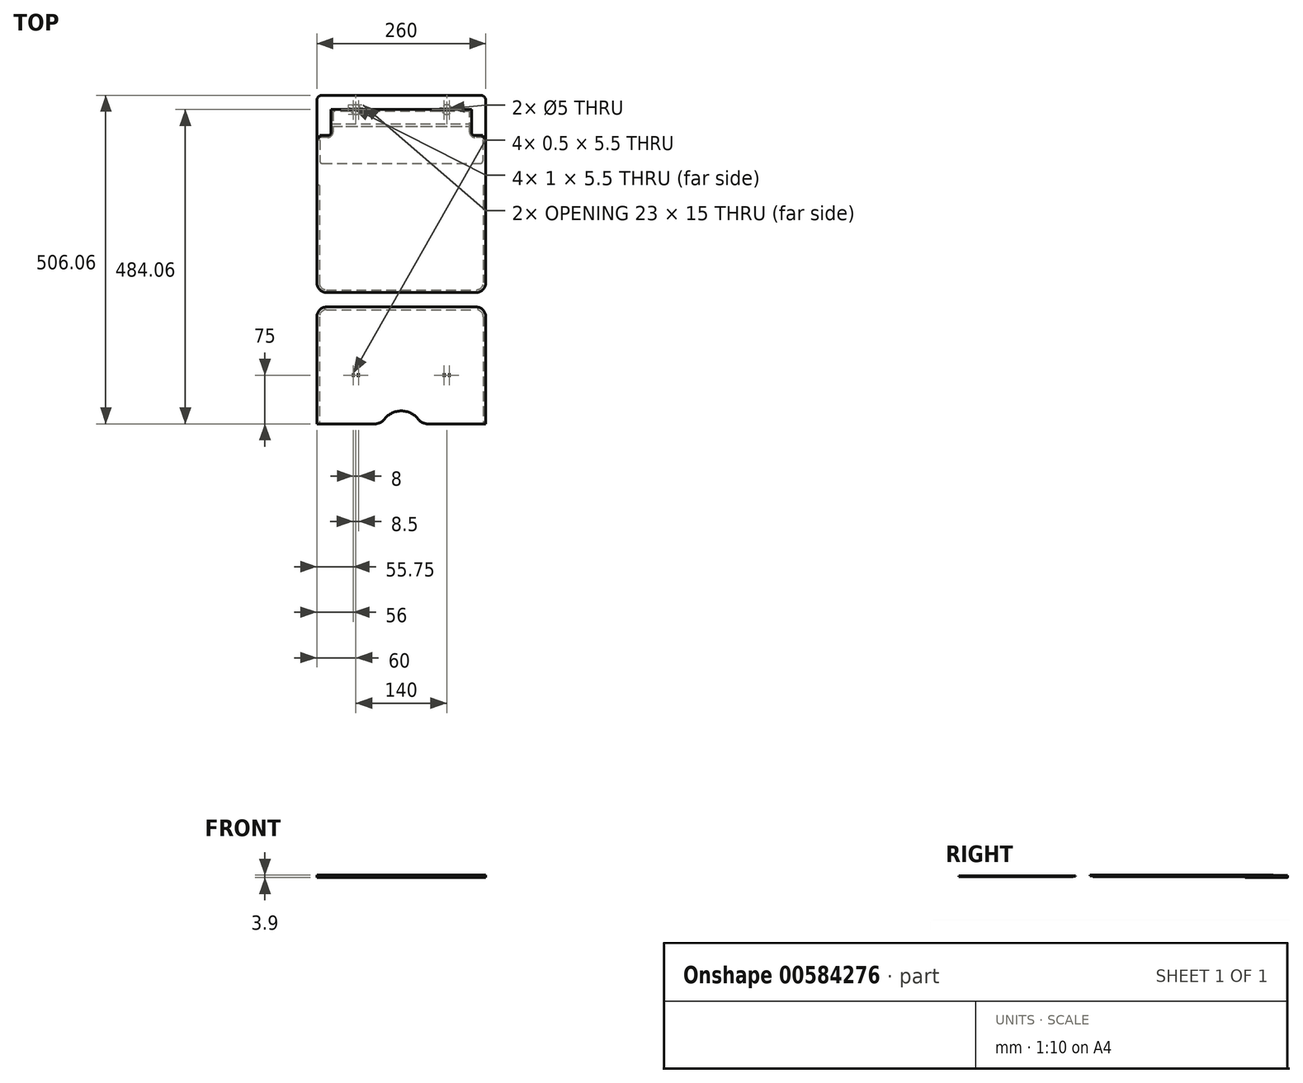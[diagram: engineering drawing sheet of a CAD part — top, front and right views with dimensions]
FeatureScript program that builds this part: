
annotation { "Feature Type Name" : "Feature", "Feature Type Description" : "" }
export const myFeature = defineFeature(function(context is Context, id is Id, definition is map)
    precondition{}
    {
        {
            var Q0;
            Q0=qCreatedBy(makeId("Top.planeOp"),FACE);
            var sketch = newSketch(context, id + "F0", { "sketchPlane" : qUnion([Q0])});
            skLineSegment(sketch, "E0.bottom", {"start": v(122, 253.03) * mm, "end": v(-122, 253.03) * mm});
            skLineSegment(sketch, "E0.top", {"start": v(-41.23, -253.03) * mm, "end": v(-130, -253.03) * mm});
            skLineSegment(sketch, "E0.left", {"start": v(130, 245.03) * mm, "end": v(130, 129.37) * mm});
            skLineSegment(sketch, "E0.right", {"start": v(-130, 245.03) * mm, "end": v(-130, 129.37) * mm});
            skPoint(sketch, "E0.middle", {"position": v(0, 0) * mm});
            skPoint(sketch, "E1", {"position": v(130, 147.97) * mm});
            skLineSegment(sketch, "E2", {"start": v(130, 188.1) * mm, "end": v(113.2, 188.1) * mm});
            skLineSegment(sketch, "E3", {"start": v(105.2, 196.1) * mm, "end": v(105.2, 228.22) * mm});
            skLineSegment(sketch, "E4", {"start": v(105.2, 228.22) * mm, "end": v(-105.2, 228.22) * mm});
            skLineSegment(sketch, "E5", {"start": v(-105.2, 228.22) * mm, "end": v(-105.2, 196.1) * mm});
            skLineSegment(sketch, "E6", {"start": v(-113.2, 188.1) * mm, "end": v(-130, 188.1) * mm});
            skLineSegment(sketch, "E7", {"start": v(-60.78, 228.22) * mm, "end": v(-60.78, 253.03) * mm, "construction": true});
            skPoint(sketch, "E8.visualSharp", {"position": v(-130, 253.03) * mm});
            skArc(sketch, "E8.filletArc", {"start": v(-122, 253.03) * mm, "mid": v(-127.66, 250.69) * mm, "end": v(-130, 245.03) * mm});
            skPoint(sketch, "E9.visualSharp", {"position": v(130, 253.03) * mm});
            skArc(sketch, "E9.filletArc", {"start": v(130, 245.03) * mm, "mid": v(127.66, 250.69) * mm, "end": v(122, 253.03) * mm});
            skPoint(sketch, "E10.visualSharp", {"position": v(105.2, 188.1) * mm});
            skArc(sketch, "E10.filletArc", {"start": v(105.2, 196.1) * mm, "mid": v(107.54, 190.43) * mm, "end": v(113.2, 188.1) * mm});
            skPoint(sketch, "E11.visualSharp", {"position": v(-105.2, 188.1) * mm});
            skArc(sketch, "E11.filletArc", {"start": v(-113.2, 188.1) * mm, "mid": v(-107.54, 190.43) * mm, "end": v(-105.2, 196.1) * mm});
            skLineSegment(sketch, "E12", {"start": v(-130, 179) * mm, "end": v(-105.2, 179) * mm, "construction": true});
            skLineSegment(sketch, "E13", {"start": v(130, 147.97) * mm, "end": v(-130, 147.97) * mm, "construction": true});
            skArc(sketch, "E14", {"start": v(25.52, -245.41) * mm, "mid": v(0, -233.03) * mm, "end": v(-25.52, -245.41) * mm});
            skPoint(sketch, "E15.newPointA", {"position": v(-30, -253.03) * mm});
            skPoint(sketch, "E15.newPointB", {"position": v(130, -253.03) * mm});
            skArc(sketch, "E15.filletArc", {"start": v(-41.23, -253.03) * mm, "mid": v(-32.5, -251.02) * mm, "end": v(-25.52, -245.41) * mm});
            skLineSegment(sketch, "E16", {"start": v(41.23, -253.03) * mm, "end": v(132.5, -253.03) * mm});
            skPoint(sketch, "E17.visualSharp", {"position": v(30, -253.03) * mm});
            skArc(sketch, "E17.filletArc", {"start": v(25.52, -245.41) * mm, "mid": v(32.5, -251.02) * mm, "end": v(41.23, -253.03) * mm});
            skLineSegment(sketch, "E18.0", {"start": v(-113.2, 191.1) * mm, "end": v(-125.5, 191.1) * mm});
            skArc(sketch, "E18.1", {"start": v(-113.2, 191.1) * mm, "mid": v(-109.66, 192.55) * mm, "end": v(-108.2, 196.1) * mm});
            skLineSegment(sketch, "E18.2", {"start": v(-108.2, 231.22) * mm, "end": v(-108.2, 196.1) * mm});
            skLineSegment(sketch, "E18.3", {"start": v(125.5, 191.1) * mm, "end": v(113.2, 191.1) * mm});
            skArc(sketch, "E18.4", {"start": v(108.2, 196.1) * mm, "mid": v(109.66, 192.55) * mm, "end": v(113.2, 191.1) * mm});
            skLineSegment(sketch, "E18.5", {"start": v(108.2, 196.1) * mm, "end": v(108.2, 231.22) * mm});
            skLineSegment(sketch, "E18.6", {"start": v(108.2, 231.22) * mm, "end": v(-108.2, 231.22) * mm});
            skLineSegment(sketch, "E19", {"start": v(-125.5, 191.1) * mm, "end": v(-125.5, 188.1) * mm});
            skLineSegment(sketch, "E20.MirrorCS", {"start": v(125.5, 191.1) * mm, "end": v(125.5, 188.1) * mm});
            skLineSegment(sketch, "E21", {"start": v(-115, -73.03) * mm, "end": v(115, -73.03) * mm});
            skLineSegment(sketch, "E22", {"start": v(-115, -50.63) * mm, "end": v(115, -50.63) * mm});
            skArc(sketch, "E23.filletArc", {"start": v(-130, -35.63) * mm, "mid": v(-125.6, -46.24) * mm, "end": v(-115, -50.63) * mm});
            skArc(sketch, "E24.filletArc", {"start": v(115, -50.63) * mm, "mid": v(125.6, -46.24) * mm, "end": v(130, -35.63) * mm});
            skLineSegment(sketch, "E25", {"start": v(-130, -88.03) * mm, "end": v(-130, -253.03) * mm});
            skLineSegment(sketch, "E26", {"start": v(130, -88.03) * mm, "end": v(130, -253.03) * mm});
            skPoint(sketch, "E27.visualSharp", {"position": v(-130, -73.03) * mm});
            skArc(sketch, "E27.filletArc", {"start": v(-115, -73.03) * mm, "mid": v(-125.6, -77.42) * mm, "end": v(-130, -88.03) * mm});
            skPoint(sketch, "E28.visualSharp", {"position": v(130, -73.03) * mm});
            skArc(sketch, "E28.filletArc", {"start": v(130, -88.03) * mm, "mid": v(125.6, -77.42) * mm, "end": v(115, -73.03) * mm});
            skLineSegment(sketch, "E29.bottom", {"start": v(-74.25, -175.28) * mm, "end": v(-73.75, -175.28) * mm});
            skLineSegment(sketch, "E29.top", {"start": v(-74.25, -180.78) * mm, "end": v(-73.75, -180.78) * mm});
            skLineSegment(sketch, "E29.left", {"start": v(-74.25, -175.28) * mm, "end": v(-74.25, -180.78) * mm});
            skLineSegment(sketch, "E29.right", {"start": v(-73.75, -175.28) * mm, "end": v(-73.75, -180.78) * mm});
            skLineSegment(sketch, "E30", {"start": v(-70, -182.22) * mm, "end": v(-70, -190.86) * mm, "construction": true});
            skPoint(sketch, "E31.orphan", {"position": v(-90.2, -187.28) * mm});
            skLineSegment(sketch, "E32.MirrorCS", {"start": v(-65.75, -180.78) * mm, "end": v(-66.25, -180.78) * mm});
            skLineSegment(sketch, "E33.MirrorCS", {"start": v(-66.25, -175.28) * mm, "end": v(-66.25, -180.78) * mm});
            skLineSegment(sketch, "E34.MirrorCS", {"start": v(-65.75, -175.28) * mm, "end": v(-65.75, -180.78) * mm});
            skLineSegment(sketch, "E35.MirrorCS", {"start": v(-65.75, -175.28) * mm, "end": v(-66.25, -175.28) * mm});
            skPoint(sketch, "E36", {"position": v(-70, -178.03) * mm});
            skLineSegment(sketch, "E37.trimOffspring", {"start": v(-73.75, -178.03) * mm, "end": v(-66.25, -178.03) * mm, "construction": true});
            skPoint(sketch, "E38.trimOffspring.end.orphan", {"position": v(-65.68, -178.03) * mm});
            skPoint(sketch, "E39.start.orphan", {"position": v(-74.32, -178.03) * mm});
            skLineSegment(sketch, "E40.MirrorCS", {"start": v(74.25, -180.78) * mm, "end": v(73.75, -180.78) * mm});
            skLineSegment(sketch, "E41.MirrorCS", {"start": v(74.25, -175.28) * mm, "end": v(73.75, -175.28) * mm});
            skLineSegment(sketch, "E42.MirrorCS", {"start": v(65.75, -175.28) * mm, "end": v(66.25, -175.28) * mm});
            skLineSegment(sketch, "E43.MirrorCS", {"start": v(65.75, -180.78) * mm, "end": v(66.25, -180.78) * mm});
            skPoint(sketch, "E44.MirrorP", {"position": v(74.32, -178.03) * mm});
            skLineSegment(sketch, "E45.MirrorCS", {"start": v(65.75, -175.28) * mm, "end": v(65.75, -180.78) * mm});
            skLineSegment(sketch, "E46.MirrorCS", {"start": v(73.75, -178.03) * mm, "end": v(66.25, -178.03) * mm, "construction": true});
            skLineSegment(sketch, "E47.MirrorCS", {"start": v(73.75, -175.28) * mm, "end": v(73.75, -180.78) * mm});
            skPoint(sketch, "E48.MirrorP", {"position": v(70, -178.03) * mm});
            skLineSegment(sketch, "E49.MirrorCS", {"start": v(74.25, -175.28) * mm, "end": v(74.25, -180.78) * mm});
            skLineSegment(sketch, "E50.MirrorCS", {"start": v(66.25, -175.28) * mm, "end": v(66.25, -180.78) * mm});
            skPoint(sketch, "E51.MirrorP", {"position": v(65.68, -178.03) * mm});
            skLineSegment(sketch, "E52", {"start": v(-130, 129.37) * mm, "end": v(130, 129.37) * mm, "construction": true});
            skLineSegment(sketch, "E53", {"start": v(-130, 129.37) * mm, "end": v(-130, -35.63) * mm});
            skLineSegment(sketch, "E54", {"start": v(130, 129.37) * mm, "end": v(130, -35.63) * mm});
            skSolve(sketch);
        }
        {
            var Q0;
            {var subQ1=sQuery(id+"F0.wireOp",EDGE,"E0.top");Q0=makeQuery(id+"F0.imprint","IMPRINT",FACE,{"disambiguationData":[TD([[makeQuery(id+"F0.imprint","IMPRINT",EDGE,{"derivedFrom":subQ1}),-1.0]])]});}
            extrude(context, id + "F1", {"entities" : qUnion([Q0]), "oppositeDirection" : true, "depth" : 0.8 * mm, "offsetDistance" : 25 * mm});
        }
        {
            var Q0;
            Q0=makeQuery(id+"F0.imprint","IMPRINT",FACE,{"disambiguationData":[TD([[makeQuery(id+"F0.imprint","IMPRINT",EDGE,{"derivedFrom":sQuery(id+"F0.wireOp",EDGE,"E3")}),1.0]])]});
            var Q1;
            Q1=makeQuery(id+"F0.imprint","IMPRINT",FACE,{"disambiguationData":[TD([[makeQuery(id+"F0.imprint","IMPRINT",EDGE,{"derivedFrom":sQuery(id+"F0.wireOp",EDGE,"E3")}),-1.0]])]});
            extrude(context, id + "F2", {"entities" : qUnion([Q0, Q1]), "depth" : 0.9 * mm, "offsetDistance" : 25 * mm});
        }
        {
            var Q0;
            Q0=makeQuery(id+"F0.imprint","IMPRINT",FACE,{"disambiguationData":[TD([[makeQuery(id+"F0.imprint","IMPRINT",EDGE,{"derivedFrom":sQuery(id+"F0.wireOp",EDGE,"E0.bottom")}),1.0]])]});
            extrude(context, id + "F3", {"entities" : qUnion([Q0]), "oppositeDirection" : true, "depth" : 0.9 * mm, "offsetDistance" : 25 * mm});
        }
        {
            var Q0;
            Q0=makeQuery(id+"F0.imprint","IMPRINT",FACE,{"disambiguationData":[TD([[makeQuery(id+"F0.imprint","IMPRINT",EDGE,{"derivedFrom":sQuery(id+"F0.wireOp",EDGE,"E3")}),-1.0]])]});
            var Q1;
            Q1=makeQuery(id+"F0.imprint","IMPRINT",FACE,{"disambiguationData":[TD([[makeQuery(id+"F0.imprint","IMPRINT",EDGE,{"derivedFrom":sQuery(id+"F0.wireOp",EDGE,"E0.bottom")}),1.0]])]});
            extrude(context, id + "F4", {"entities" : qUnion([Q0, Q1]), "depth" : 0.6 * mm, "offsetDistance" : 25 * mm});
        }
        {
            var Q0;
            Q0=makeQuery(id+"F3.opExtrude","CAP_FACE",FACE,{"disambiguationData":[OSD([sQuery(id+"F0.wireOp",EDGE,"E0.bottom"),sQuery(id+"F0.wireOp",EDGE,"E0.left"),sQuery(id+"F0.wireOp",EDGE,"E0.right"),sQuery(id+"F0.wireOp",EDGE,"E2"),sQuery(id+"F0.wireOp",EDGE,"E6"),sQuery(id+"F0.wireOp",EDGE,"E8.filletArc"),sQuery(id+"F0.wireOp",EDGE,"E9.filletArc"),sQuery(id+"F0.wireOp",EDGE,"E18.0"),sQuery(id+"F0.wireOp",EDGE,"E18.2"),sQuery(id+"F0.wireOp",EDGE,"E18.3"),sQuery(id+"F0.wireOp",EDGE,"E18.5"),sQuery(id+"F0.wireOp",EDGE,"E18.6"),sQuery(id+"F0.wireOp",EDGE,"E19"),sQuery(id+"F0.wireOp",EDGE,"E20.MirrorCS")])],"isStart":false});
            var sketch = newSketch(context, id + "F5", { "sketchPlane" : qUnion([Q0])});
            skLineSegment(sketch, "E55.0", {"start": v(-130, -245.03) * mm, "end": v(-130, -188.1) * mm});
            skArc(sketch, "E56.0", {"start": v(-122, -253.03) * mm, "mid": v(-127.66, -250.69) * mm, "end": v(-130, -245.03) * mm});
            skLineSegment(sketch, "E57.0", {"start": v(122, -253.03) * mm, "end": v(-122, -253.03) * mm});
            skArc(sketch, "E58.0", {"start": v(130, -245.03) * mm, "mid": v(127.66, -250.69) * mm, "end": v(122, -253.03) * mm});
            skLineSegment(sketch, "E59.0", {"start": v(130, -245.03) * mm, "end": v(130, -188.1) * mm});
            skPoint(sketch, "E60.orphan", {"position": v(-130, -129.37) * mm});
            skPoint(sketch, "E61.orphan", {"position": v(130, -129.37) * mm});
            skLineSegment(sketch, "E62.0", {"start": v(-125.5, -191.1) * mm, "end": v(-125.5, -188.1) * mm});
            skLineSegment(sketch, "E63", {"start": v(-125.5, -183.96) * mm, "end": v(-125.5, -151.97) * mm});
            skArc(sketch, "E64", {"start": v(-125.86, -184.36) * mm, "mid": v(-128.28, -185.57) * mm, "end": v(-129.25, -188.1) * mm});
            skPoint(sketch, "E65.newPointB", {"position": v(-129.25, -188.1) * mm});
            skArc(sketch, "E66.filletArc", {"start": v(-125.86, -184.36) * mm, "mid": v(-125.6, -184.23) * mm, "end": v(-125.5, -183.96) * mm});
            skLineSegment(sketch, "E67.0", {"start": v(0, -147.97) * mm, "end": v(-121.5, -147.97) * mm});
            skPoint(sketch, "E68.newPointB", {"position": v(-130, -147.97) * mm});
            skArc(sketch, "E68.filletArc", {"start": v(-121.5, -147.97) * mm, "mid": v(-124.33, -149.14) * mm, "end": v(-125.5, -151.97) * mm});
            skPoint(sketch, "E69.orphan", {"position": v(130, -147.97) * mm});
            skLineSegment(sketch, "E70.MirrorCS", {"start": v(0, -147.97) * mm, "end": v(121.5, -147.97) * mm});
            skArc(sketch, "E71.MirrorCS", {"start": v(121.5, -147.97) * mm, "mid": v(124.33, -149.14) * mm, "end": v(125.5, -151.97) * mm});
            skLineSegment(sketch, "E72.MirrorCS", {"start": v(125.5, -183.96) * mm, "end": v(125.5, -151.97) * mm});
            skArc(sketch, "E73.MirrorCS", {"start": v(125.86, -184.36) * mm, "mid": v(125.6, -184.23) * mm, "end": v(125.5, -183.96) * mm});
            skArc(sketch, "E74.MirrorCS", {"start": v(125.86, -184.36) * mm, "mid": v(128.28, -185.57) * mm, "end": v(129.25, -188.1) * mm});
            skLineSegment(sketch, "E75", {"start": v(-130, -188.1) * mm, "end": v(-129.25, -188.1) * mm});
            skLineSegment(sketch, "E76", {"start": v(129.25, -188.1) * mm, "end": v(130, -188.1) * mm});
            skSolve(sketch);
        }
        {
            var Q0;
            Q0 = qSketchRegion(id + "F5", true);
            extrude(context, id + "F6", {"entities" : qUnion([Q0]), "depth" : 0.6 * mm, "offsetDistance" : 25 * mm});
        }
        {
            var Q0;
            Q0=makeQuery(id+"F6.opExtrude","CAP_FACE",FACE,{"disambiguationData":[OSD([sQuery(id+"F5.wireOp",EDGE,"E55.0"),sQuery(id+"F5.wireOp",EDGE,"E56.0"),sQuery(id+"F5.wireOp",EDGE,"E57.0"),sQuery(id+"F5.wireOp",EDGE,"E58.0"),sQuery(id+"F5.wireOp",EDGE,"E59.0"),sQuery(id+"F5.wireOp",EDGE,"mqd3fcgL-vkYM-jt8C-SEZb-QTAqxbzKtnkH"),sQuery(id+"F5.wireOp",EDGE,"E63"),sQuery(id+"F5.wireOp",EDGE,"E64"),sQuery(id+"F5.wireOp",EDGE,"E65.filletArc"),sQuery(id+"F5.wireOp",EDGE,"E66.filletArc"),sQuery(id+"F5.wireOp",EDGE,"E67.0"),sQuery(id+"F5.wireOp",EDGE,"E68.filletArc"),sQuery(id+"F5.wireOp",EDGE,"E70.MirrorCS"),sQuery(id+"F5.wireOp",EDGE,"E71.MirrorCS"),sQuery(id+"F5.wireOp",EDGE,"E72.MirrorCS"),sQuery(id+"F5.wireOp",EDGE,"E73.MirrorCS"),sQuery(id+"F5.wireOp",EDGE,"E74.MirrorCS"),sQuery(id+"F5.wireOp",EDGE,"eea31a7d-e614-436a-bde2-b2130c57034b0.MirrorCS"),sQuery(id+"F5.wireOp",EDGE,"bd1179cf-cb36-4206-b0af-3bf9bbb72a3d0.MirrorCS")])],"isStart":false});
            var sketch = newSketch(context, id + "F7", { "sketchPlane" : qUnion([Q0])});
            skLineSegment(sketch, "E77.0.0", {"start": v(-125.5, -188.1) * mm, "end": v(-125.5, -191.1) * mm});
            skLineSegment(sketch, "E77.0.1", {"start": v(-125.5, -191.1) * mm, "end": v(-113.2, -191.1) * mm});
            skArc(sketch, "E77.0.2", {"start": v(-113.2, -191.1) * mm, "mid": v(-109.66, -192.55) * mm, "end": v(-108.2, -196.1) * mm});
            skLineSegment(sketch, "E77.0.3", {"start": v(-108.2, -196.1) * mm, "end": v(-108.2, -209.03) * mm});
            skLineSegment(sketch, "E77.0.5", {"start": v(108.2, -209.03) * mm, "end": v(108.2, -196.1) * mm});
            skArc(sketch, "E77.0.6", {"start": v(108.2, -196.1) * mm, "mid": v(109.66, -192.55) * mm, "end": v(113.2, -191.1) * mm});
            skLineSegment(sketch, "E77.0.7", {"start": v(113.2, -191.1) * mm, "end": v(125.5, -191.1) * mm});
            skLineSegment(sketch, "E77.0.8", {"start": v(125.5, -191.1) * mm, "end": v(125.5, -188.1) * mm});
            skLineSegment(sketch, "E77.0.9", {"start": v(125.5, -188.1) * mm, "end": v(130, -188.1) * mm});
            skLineSegment(sketch, "E77.0.10", {"start": v(130, -188.1) * mm, "end": v(130, -245.03) * mm});
            skArc(sketch, "E77.0.11", {"start": v(130, -245.03) * mm, "mid": v(127.66, -250.69) * mm, "end": v(122, -253.03) * mm});
            skLineSegment(sketch, "E77.0.12", {"start": v(122, -253.03) * mm, "end": v(-122, -253.03) * mm});
            skArc(sketch, "E77.0.13", {"start": v(-122, -253.03) * mm, "mid": v(-127.66, -250.69) * mm, "end": v(-130, -245.03) * mm});
            skLineSegment(sketch, "E77.0.14", {"start": v(-130, -245.03) * mm, "end": v(-130, -188.1) * mm});
            skLineSegment(sketch, "E77.0.15", {"start": v(-130, -188.1) * mm, "end": v(-125.5, -188.1) * mm});
            skLineSegment(sketch, "E78", {"start": v(-108.2, -209.03) * mm, "end": v(108.2, -209.03) * mm});
            skPoint(sketch, "E77.0.4.end.orphan", {"position": v(108.2, -231.22) * mm});
            skPoint(sketch, "E77.0.4.start.orphan", {"position": v(-108.2, -231.22) * mm});
            skArc(sketch, "E79", {"start": v(-77.07, -233.53) * mm, "mid": v(-70, -238.53) * mm, "end": v(-62.93, -233.53) * mm});
            skLineSegment(sketch, "E80", {"start": v(-79, -231.03) * mm, "end": v(-61, -231.03) * mm, "construction": true});
            skLineSegment(sketch, "E81", {"start": v(-70, -233.39) * mm, "end": v(-70, -223.53) * mm, "construction": true});
            skArc(sketch, "E82.0.startCap", {"start": v(-79, -233.53) * mm, "mid": v(-81.5, -231.03) * mm, "end": v(-79, -228.53) * mm});
            skArc(sketch, "E82.0.endCap", {"start": v(-61, -228.53) * mm, "mid": v(-58.5, -231.03) * mm, "end": v(-61, -233.53) * mm});
            skLineSegment(sketch, "E82.0.left", {"start": v(-79, -228.53) * mm, "end": v(-77.07, -228.53) * mm});
            skLineSegment(sketch, "E82.0.right", {"start": v(-79, -233.53) * mm, "end": v(-77.07, -233.53) * mm});
            skLineSegment(sketch, "E83.trimOffspring", {"start": v(-62.93, -228.53) * mm, "end": v(-61, -228.53) * mm});
            skLineSegment(sketch, "E84.trimOffspring", {"start": v(-62.93, -233.53) * mm, "end": v(-61, -233.53) * mm});
            skArc(sketch, "E85.trimOffspring", {"start": v(-62.93, -228.53) * mm, "mid": v(-70, -223.53) * mm, "end": v(-77.07, -228.53) * mm});
            skArc(sketch, "E86.MirrorCS", {"start": v(77.07, -233.53) * mm, "mid": v(70, -238.53) * mm, "end": v(62.93, -233.53) * mm});
            skLineSegment(sketch, "E87.MirrorCS", {"start": v(79, -233.53) * mm, "end": v(77.07, -233.53) * mm});
            skArc(sketch, "E88.MirrorCS", {"start": v(79, -233.53) * mm, "mid": v(81.5, -231.03) * mm, "end": v(79, -228.53) * mm});
            skLineSegment(sketch, "E89.MirrorCS", {"start": v(79, -228.53) * mm, "end": v(77.07, -228.53) * mm});
            skArc(sketch, "E90.MirrorCS", {"start": v(62.93, -228.53) * mm, "mid": v(70, -223.53) * mm, "end": v(77.07, -228.53) * mm});
            skLineSegment(sketch, "E91.MirrorCS", {"start": v(62.93, -228.53) * mm, "end": v(61, -228.53) * mm});
            skArc(sketch, "E92.MirrorCS", {"start": v(61, -228.53) * mm, "mid": v(58.5, -231.03) * mm, "end": v(61, -233.53) * mm});
            skLineSegment(sketch, "E93.MirrorCS", {"start": v(62.93, -233.53) * mm, "end": v(61, -233.53) * mm});
            skSolve(sketch);
        }
        {
            var Q0;
            {var subQ1=sQuery(id+"F7.wireOp",EDGE,"E77.0.0");Q0=makeQuery(id+"F7.imprint","IMPRINT",FACE,{"disambiguationData":[TD([[makeQuery(id+"F7.imprint","IMPRINT",EDGE,{"derivedFrom":subQ1}),-1.0]])]});}
            extrude(context, id + "F8", {"entities" : qUnion([Q0]), "depth" : 0.9 * mm, "offsetDistance" : 25 * mm});
        }
        {
            var Q0;
            Q0=makeQuery(id+"F8.opExtrude","CAP_FACE",FACE,{"disambiguationData":[OSD([sQuery(id+"F5.wireOp",EDGE,"mqd3fcgL-vkYM-jt8C-SEZb-QTAqxbzKtnkH"),sQuery(id+"F5.wireOp",EDGE,"E65.filletArc"),sQuery(id+"F5.wireOp",EDGE,"eea31a7d-e614-436a-bde2-b2130c57034b0.MirrorCS"),sQuery(id+"F5.wireOp",EDGE,"bd1179cf-cb36-4206-b0af-3bf9bbb72a3d0.MirrorCS"),sQuery(id+"F7.wireOp",EDGE,"E77.0.0"),sQuery(id+"F7.wireOp",EDGE,"E77.0.1"),sQuery(id+"F7.wireOp",EDGE,"E77.0.2"),sQuery(id+"F7.wireOp",EDGE,"E77.0.3"),sQuery(id+"F7.wireOp",EDGE,"E77.0.5"),sQuery(id+"F7.wireOp",EDGE,"E77.0.6"),sQuery(id+"F7.wireOp",EDGE,"E77.0.7"),sQuery(id+"F7.wireOp",EDGE,"E77.0.8"),sQuery(id+"F7.wireOp",EDGE,"E77.0.9"),sQuery(id+"F7.wireOp",EDGE,"E77.0.10"),sQuery(id+"F7.wireOp",EDGE,"E77.0.11"),sQuery(id+"F7.wireOp",EDGE,"E77.0.12"),sQuery(id+"F7.wireOp",EDGE,"E77.0.13"),sQuery(id+"F7.wireOp",EDGE,"E77.0.14"),sQuery(id+"F7.wireOp",EDGE,"E77.0.15"),sQuery(id+"F7.wireOp",EDGE,"E78"),sQuery(id+"F7.wireOp",EDGE,"E79"),sQuery(id+"F7.wireOp",EDGE,"E82.0.startCap"),sQuery(id+"F7.wireOp",EDGE,"E82.0.endCap"),sQuery(id+"F7.wireOp",EDGE,"E82.0.left"),sQuery(id+"F7.wireOp",EDGE,"E82.0.right"),sQuery(id+"F7.wireOp",EDGE,"E83.trimOffspring"),sQuery(id+"F7.wireOp",EDGE,"E84.trimOffspring"),sQuery(id+"F7.wireOp",EDGE,"E85.trimOffspring"),sQuery(id+"F7.wireOp",EDGE,"E86.MirrorCS"),sQuery(id+"F7.wireOp",EDGE,"E87.MirrorCS"),sQuery(id+"F7.wireOp",EDGE,"E88.MirrorCS"),sQuery(id+"F7.wireOp",EDGE,"E89.MirrorCS"),sQuery(id+"F7.wireOp",EDGE,"E90.MirrorCS"),sQuery(id+"F7.wireOp",EDGE,"E91.MirrorCS"),sQuery(id+"F7.wireOp",EDGE,"E92.MirrorCS"),sQuery(id+"F7.wireOp",EDGE,"E93.MirrorCS")])],"isStart":false});
            var sketch = newSketch(context, id + "F9", { "sketchPlane" : qUnion([Q0])});
            skLineSegment(sketch, "E94.0.0", {"start": v(-130, -245.03) * mm, "end": v(-130, -188.1) * mm});
            skLineSegment(sketch, "E94.0.1", {"start": v(-130, -188.1) * mm, "end": v(-113.2, -188.1) * mm});
            skArc(sketch, "E94.0.2", {"start": v(-113.2, -188.1) * mm, "mid": v(-107.54, -190.43) * mm, "end": v(-105.2, -196.1) * mm});
            skLineSegment(sketch, "E94.0.3", {"start": v(-105.2, -196.1) * mm, "end": v(-105.2, -205.03) * mm});
            skLineSegment(sketch, "E94.0.5", {"start": v(105.2, -205.03) * mm, "end": v(105.2, -196.1) * mm});
            skArc(sketch, "E94.0.6", {"start": v(105.2, -196.1) * mm, "mid": v(107.54, -190.43) * mm, "end": v(113.2, -188.1) * mm});
            skLineSegment(sketch, "E94.0.7", {"start": v(113.2, -188.1) * mm, "end": v(130, -188.1) * mm});
            skLineSegment(sketch, "E94.0.8", {"start": v(130, -188.1) * mm, "end": v(130, -245.03) * mm});
            skArc(sketch, "E94.0.9", {"start": v(130, -245.03) * mm, "mid": v(127.66, -250.69) * mm, "end": v(122, -253.03) * mm});
            skLineSegment(sketch, "E94.0.10", {"start": v(122, -253.03) * mm, "end": v(-122, -253.03) * mm});
            skArc(sketch, "E94.0.11", {"start": v(-122, -253.03) * mm, "mid": v(-127.66, -250.69) * mm, "end": v(-130, -245.03) * mm});
            skLineSegment(sketch, "E95", {"start": v(-105.2, -205.03) * mm, "end": v(105.2, -205.03) * mm});
            skPoint(sketch, "E95.startSnap0", {"position": v(-110.7, -205.03) * mm});
            skPoint(sketch, "E94.0.4.end.orphan", {"position": v(105.2, -228.22) * mm});
            skPoint(sketch, "E94.0.4.start.orphan", {"position": v(-105.2, -228.22) * mm});
            skArc(sketch, "E96.0", {"start": v(-62.93, -228.53) * mm, "mid": v(-70, -223.53) * mm, "end": v(-77.07, -228.53) * mm, "construction": true});
            skCircle(sketch, "E97", {"center": v(-70, -231.03) * mm, "radius": 2.5 * mm});
            skLineSegment(sketch, "E98.bottom", {"start": v(-74.75, -228.28) * mm, "end": v(-73.75, -228.28) * mm});
            skLineSegment(sketch, "E98.top", {"start": v(-74.75, -233.78) * mm, "end": v(-73.75, -233.78) * mm});
            skLineSegment(sketch, "E98.left", {"start": v(-74.75, -228.28) * mm, "end": v(-74.75, -233.78) * mm});
            skLineSegment(sketch, "E98.right", {"start": v(-73.75, -228.28) * mm, "end": v(-73.75, -233.78) * mm});
            skLineSegment(sketch, "E99", {"start": v(-70, -231.03) * mm, "end": v(-70, -223.53) * mm, "construction": true});
            skLineSegment(sketch, "E100.MirrorCS", {"start": v(-65.25, -233.78) * mm, "end": v(-66.25, -233.78) * mm});
            skLineSegment(sketch, "E101.MirrorCS", {"start": v(-65.25, -228.28) * mm, "end": v(-65.25, -233.78) * mm});
            skLineSegment(sketch, "E102.MirrorCS", {"start": v(-66.25, -228.28) * mm, "end": v(-66.25, -233.78) * mm});
            skLineSegment(sketch, "E103.MirrorCS", {"start": v(-65.25, -228.28) * mm, "end": v(-66.25, -228.28) * mm});
            skLineSegment(sketch, "E104", {"start": v(-72.5, -231.03) * mm, "end": v(-67.5, -231.03) * mm, "construction": true});
            skLineSegment(sketch, "E105.MirrorCS", {"start": v(74.75, -228.28) * mm, "end": v(73.75, -228.28) * mm});
            skLineSegment(sketch, "E106.MirrorCS", {"start": v(65.25, -233.78) * mm, "end": v(66.25, -233.78) * mm});
            skLineSegment(sketch, "E107.MirrorCS", {"start": v(65.25, -228.28) * mm, "end": v(66.25, -228.28) * mm});
            skLineSegment(sketch, "E108.MirrorCS", {"start": v(74.75, -233.78) * mm, "end": v(73.75, -233.78) * mm});
            skLineSegment(sketch, "E109.MirrorCS", {"start": v(65.25, -228.28) * mm, "end": v(65.25, -233.78) * mm});
            skLineSegment(sketch, "E110.MirrorCS", {"start": v(72.5, -231.03) * mm, "end": v(67.5, -231.03) * mm, "construction": true});
            skLineSegment(sketch, "E111.MirrorCS", {"start": v(74.75, -228.28) * mm, "end": v(74.75, -233.78) * mm});
            skLineSegment(sketch, "E112.MirrorCS", {"start": v(73.75, -228.28) * mm, "end": v(73.75, -233.78) * mm});
            skCircle(sketch, "E113.MirrorC", {"center": v(70, -231.03) * mm, "radius": 2.5 * mm});
            skLineSegment(sketch, "E114.MirrorCS", {"start": v(66.25, -228.28) * mm, "end": v(66.25, -233.78) * mm});
            skSolve(sketch);
        }
        {
            var Q0;
            Q0 = qSketchRegion(id + "F9", true);
            extrude(context, id + "F10", {"entities" : qUnion([Q0]), "depth" : 0.6 * mm, "offsetDistance" : 25 * mm});
        }
        {
            var Q0;
            Q0=makeQuery(id+"F1.opExtrude","CAP_FACE",FACE,{"disambiguationData":[OSD([sQuery(id+"F0.wireOp",EDGE,"E0.top"),sQuery(id+"F0.wireOp",EDGE,"E0.left"),sQuery(id+"F0.wireOp",EDGE,"E0.right"),sQuery(id+"F0.wireOp",EDGE,"E14"),sQuery(id+"F0.wireOp",EDGE,"E15.filletArc"),sQuery(id+"F0.wireOp",EDGE,"E16"),sQuery(id+"F0.wireOp",EDGE,"E17.filletArc"),sQuery(id+"F0.wireOp",EDGE,"E21")])],"isStart":false});
            var sketch = newSketch(context, id + "F11", { "sketchPlane" : qUnion([Q0])});
            skLineSegment(sketch, "E115.0.2", {"start": v(126, 253.03) * mm, "end": v(41.23, 253.03) * mm});
            skArc(sketch, "E115.0.3", {"start": v(41.23, 253.03) * mm, "mid": v(32.5, 251.02) * mm, "end": v(25.52, 245.41) * mm});
            skArc(sketch, "E115.0.4", {"start": v(25.52, 245.41) * mm, "mid": v(0, 233.03) * mm, "end": v(-25.52, 245.41) * mm});
            skArc(sketch, "E115.0.5", {"start": v(-25.52, 245.41) * mm, "mid": v(-32.5, 251.02) * mm, "end": v(-41.23, 253.03) * mm});
            skLineSegment(sketch, "E115.0.6", {"start": v(-41.23, 253.03) * mm, "end": v(-126, 253.03) * mm});
            skLineSegment(sketch, "E116.0.0", {"start": v(130, -188.1) * mm, "end": v(125.5, -188.1) * mm});
            skLineSegment(sketch, "E116.0.1", {"start": v(125.5, -188.1) * mm, "end": v(125.5, -191.1) * mm});
            skLineSegment(sketch, "E116.0.2", {"start": v(125.5, -191.1) * mm, "end": v(113.2, -191.1) * mm});
            skArc(sketch, "E116.0.3", {"start": v(113.2, -191.1) * mm, "mid": v(109.66, -192.55) * mm, "end": v(108.2, -196.1) * mm});
            skLineSegment(sketch, "E116.0.4", {"start": v(108.2, -196.1) * mm, "end": v(108.2, -205.03) * mm});
            skLineSegment(sketch, "E116.0.6", {"start": v(-108.2, -205.03) * mm, "end": v(-108.2, -196.1) * mm});
            skArc(sketch, "E116.0.7", {"start": v(-108.2, -196.1) * mm, "mid": v(-109.66, -192.55) * mm, "end": v(-113.2, -191.1) * mm});
            skLineSegment(sketch, "E116.0.8", {"start": v(-113.2, -191.1) * mm, "end": v(-125.5, -191.1) * mm});
            skLineSegment(sketch, "E116.0.9", {"start": v(-125.5, -191.1) * mm, "end": v(-125.5, -188.1) * mm});
            skLineSegment(sketch, "E116.0.10", {"start": v(-125.5, -188.1) * mm, "end": v(-130, -188.1) * mm});
            skLineSegment(sketch, "E116.0.11", {"start": v(-130, -188.1) * mm, "end": v(-130, -114.37) * mm});
            skLineSegment(sketch, "E116.0.13", {"start": v(130, -114.37) * mm, "end": v(130, -188.1) * mm});
            skLineSegment(sketch, "E117", {"start": v(-126, -114.37) * mm, "end": v(-130, -114.37) * mm});
            skLineSegment(sketch, "E118.MirrorCS", {"start": v(126, -114.37) * mm, "end": v(130, -114.37) * mm});
            skPoint(sketch, "E115.0.7.start.orphan", {"position": v(-41.23, 253.03) * mm});
            skPoint(sketch, "E115.0.1.end.orphan", {"position": v(132.5, 253.03) * mm});
            skPoint(sketch, "E119.orphan", {"position": v(-115, 73.03) * mm});
            skPoint(sketch, "E120.orphan", {"position": v(115, 50.63) * mm});
            skLineSegment(sketch, "E121.0", {"start": v(126, -236.93) * mm, "end": v(126, -191.1) * mm});
            skLineSegment(sketch, "E121.1", {"start": v(-126, -114.37) * mm, "end": v(-126, 35.63) * mm});
            skArc(sketch, "E121.2", {"start": v(-126, 35.63) * mm, "mid": v(-122.78, 43.4) * mm, "end": v(-115, 46.63) * mm});
            skLineSegment(sketch, "E121.3", {"start": v(-115, 46.63) * mm, "end": v(115, 46.63) * mm});
            skArc(sketch, "E121.4", {"start": v(115, 46.63) * mm, "mid": v(122.78, 43.4) * mm, "end": v(126, 35.63) * mm});
            skLineSegment(sketch, "E122.trimOffspring", {"start": v(126, -114.37) * mm, "end": v(126, 35.63) * mm});
            skPoint(sketch, "E123.orphan", {"position": v(-130, -188.1) * mm});
            skLineSegment(sketch, "E124.0", {"start": v(-126, 88.03) * mm, "end": v(-126, 253.03) * mm});
            skLineSegment(sketch, "E124.1", {"start": v(126, 88.03) * mm, "end": v(126, 253.03) * mm});
            skArc(sketch, "E124.2", {"start": v(126, 88.03) * mm, "mid": v(122.78, 80.25) * mm, "end": v(115, 77.03) * mm});
            skLineSegment(sketch, "E124.3", {"start": v(-115, 77.03) * mm, "end": v(115, 77.03) * mm});
            skArc(sketch, "E124.4", {"start": v(-115, 77.03) * mm, "mid": v(-122.78, 80.25) * mm, "end": v(-126, 88.03) * mm});
            skLineSegment(sketch, "E125.0", {"start": v(-108.2, -205.03) * mm, "end": v(108.2, -205.03) * mm});
            skPoint(sketch, "E126.orphan", {"position": v(105.2, -205.03) * mm});
            skPoint(sketch, "E127.orphan", {"position": v(-105.2, -205.03) * mm});
            skPoint(sketch, "E116.0.5.end.orphan", {"position": v(-108.2, -231.22) * mm});
            skPoint(sketch, "E128.orphan", {"position": v(108.2, -231.22) * mm});
            skSolve(sketch);
        }
        {
            var Q0;
            Q0 = qSketchRegion(id + "F11", true);
            extrude(context, id + "F12", {"entities" : qUnion([Q0]), "depth" : 0.6 * mm, "offsetDistance" : 25 * mm});
        }
    });
